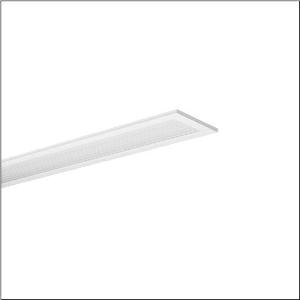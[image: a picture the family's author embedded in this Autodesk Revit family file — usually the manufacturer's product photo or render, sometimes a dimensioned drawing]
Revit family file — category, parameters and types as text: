
# Revit family: apollon_r__21_linear_51mq15wm2414_8f06
name_source: partatom
category: Lighting Fixtures
units: mm (PartAtom-declared; Revit-internal decimal feet)

## family parameters
Cut with Voids When Loaded = No
Host = Face
Light Source = No
Part Type = Normal
Room Calculation Point = No
Round Connector Dimension = Use Diameter
Shared = No

## types (1)
- --- (1 x LED, 4290 lm, 29.7 W, 4000K)
    Apparent Load = 30 VA
    CIE Flux Codes = 66 89 97 100 100
    Color Rendering = 80
    Color Temperature = 4000K
    Default Elevation = 1800 mm
    Description = Apollon® 21 linear, office luminaire, primary optical cover: micro prismatic cover, of PMMA, CAT 2 (L<= 3000cd/m²), light emission: direct distribution, primary light characteristic: symmetric, installation type: lay-in mounting, LED, rated luminous flux: 2.540lm, luminous efficacy: 147lm/W, light colour: 840, colour temperature: 4000K, with terminal, 3-pole, mains connection: 220..240V, AC/DC, 0/50..60Hz, rated input power: 17.3W, housing, of aluminium, coated, traffic white (RAL 9016), length: 1.245mm, width: 179mm, height: 30mm, housing upper side, of sheet steel, galvanised, protection rating (complete): IP20, protection rating (lamp compartment, on room side): IP50, insulation class (complete): insulation class II (safety insulation), certification: CE, ENEC, impact resistance: IK03, permissible operating ambient temperature: -20..+45°C, permissible storage temperature: -40..+80°C, packaging unit: 1 piece
    Height = 0 mm  [stored 0 ft]
    Lamp = 1 x LED
    Lamp Light Flux = 4290 lm
    Lamp Power = 29.7 W
    Lamp count = 1
    Length = 1245 mm
    Luminous efficacy = 144 lm/W
    Manufacturer = Siteco
    ModVariant = No
    Model = 51MQ15WM2414
    Mounting Place = Ceiling
    Mounting Type = Recessed
    Number of Poles = 1
    OnlyDefault = Yes
    Power Factor = 1
    Product Name = Apollon® 21 linear
    Product group = office luminaire | ceiling recessed
    ProductGroupID = 401
    Protection Class = Protection class II
    Protection Degree = IP 20
    RLX_Detail_Level = 1
    RLX_Emergency_Light_Flux = 0 lm
    RLX_Emergency_Type = 0
    RLX_Emergency_Type_DB = No
    RlxData = <blob elided: 13825 chars, md5=2fe67e64>
    Socket = socket
    Standby Power = 0 W
    System Light Flux = 4290 lm
    System Power = 30 W
    Type Comments = factory setting: luminous flux: 100 % | (ON | ON | ON) | 700 mA
    Type Image = l_1291018.jpg
    URL = http://relux.com
    VarID = @adj_026909
    Voltage = 0 V
    Weight = 0.00 kg
    Width = 179 mm

note: [stored X ft] marks values corroborated as IEEE doubles in the binary element streams (Revit-internal decimal feet)

## geometry (parser evidence)
native form markers: Sweep x13
no freeform markers — native parametric forms only
